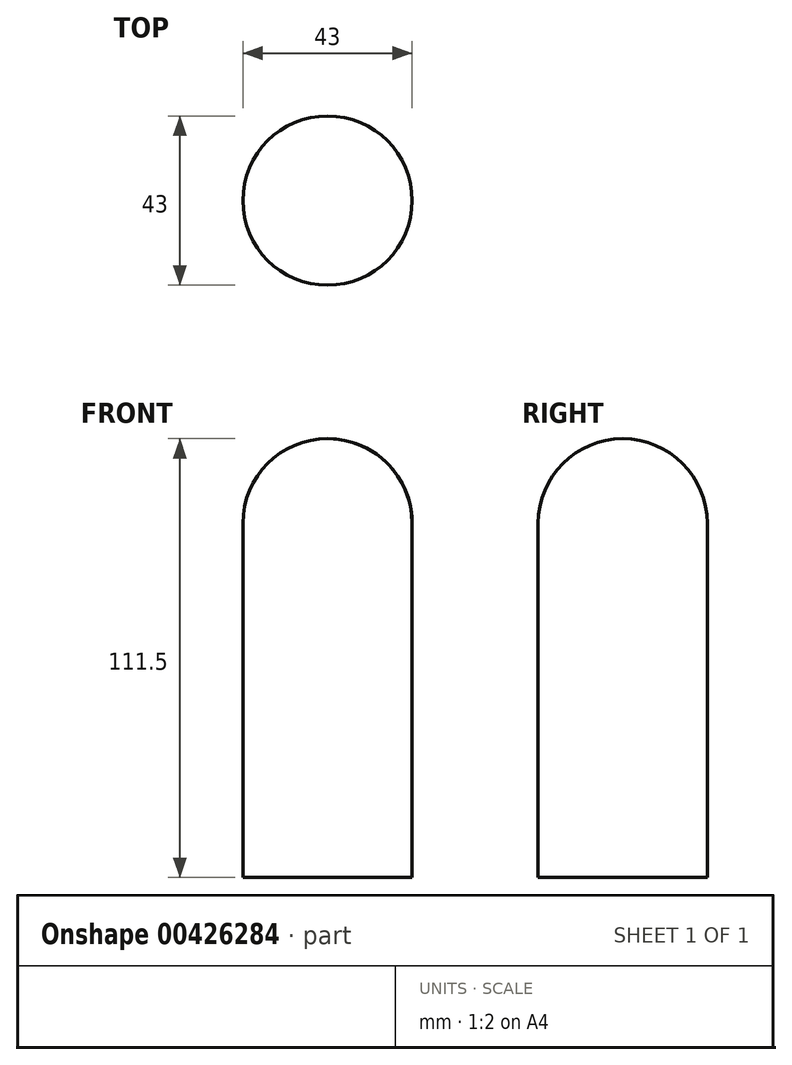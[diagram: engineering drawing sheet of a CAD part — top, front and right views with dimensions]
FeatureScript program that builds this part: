
annotation { "Feature Type Name" : "Feature", "Feature Type Description" : "" }
export const myFeature = defineFeature(function(context is Context, id is Id, definition is map)
    precondition{}
    {
        {
            var Q0;
            Q0=qCreatedBy(makeId("Front.planeOp"),FACE);
            var sketch = newSketch(context, id + "F0", { "sketchPlane" : qUnion([Q0])});
            skLineSegment(sketch, "E0", {"start": v(0, 90) * mm, "end": v(0, -97.05) * mm, "construction": true});
            skLineSegment(sketch, "E1", {"start": v(0, 0) * mm, "end": v(21.5, 0) * mm});
            skLineSegment(sketch, "E2", {"start": v(21.5, 0) * mm, "end": v(21.5, 90) * mm});
            skArc(sketch, "E3", {"start": v(21.5, 90) * mm, "mid": v(15.2, 105.2) * mm, "end": v(0, 111.5) * mm});
            skLineSegment(sketch, "E4", {"start": v(0, 90) * mm, "end": v(0, 111.5) * mm});
            skLineSegment(sketch, "E5", {"start": v(0, 90) * mm, "end": v(0, 0) * mm});
            skSolve(sketch);
        }
        {
            var Q0;
            Q0 = qSketchRegion(id + "F0", true);
            var Q1;
            Q1=sQuery(id+"F0.wireOp",EDGE,"E0");
            revolve(context, id + "F1", {"entities" : qUnion([Q0]), "axis" : qUnion([Q1]), "revolveType" : RevolveType.FULL});
        }
    });
